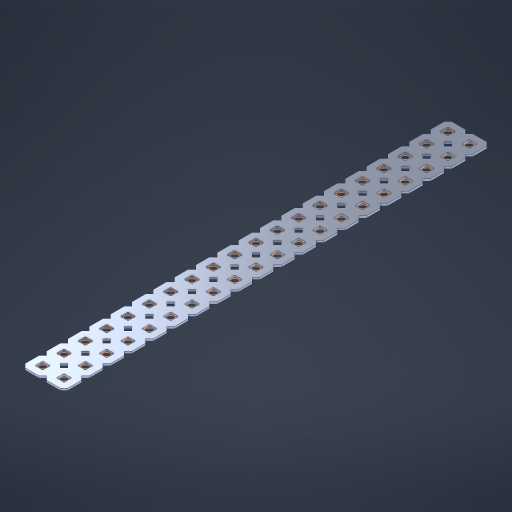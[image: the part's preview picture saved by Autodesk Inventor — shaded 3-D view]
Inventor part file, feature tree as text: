
AUTODESK INVENTOR PART (.ipt)
format: ipt  version: 2023 (Build 270158000, 158)  size: 716,800 bytes
history: native  units: in
note: dims shown in document units (in); Inventor stores cm internally (conversion verified against a paired STEP export)
features: other x41, extrude x39, sketch x2, pattern_linear x1
ambient origin geometry x8: Origin, YZ Plane, XZ Plane, XY Plane, X Axis, Y Axis, Z Axis, Center Point
bodies: Solid1 (feature_tree), Body (feature_tree)
feature tree (83):
  pattern_linear  "Rectangular Pattern1"  Spacing1=0.09in  [1 undecoded]
  sketch  "Sketch1"  dims[d1=0.5in]
  sketch  "Sketch2"  dims[d2=0.182in d3=0.09in d4=0.09in d5=0.09in d6=0.09in d7=0.09in d8=0.09in d9=0.09in d10=0.09in d11=0.02in d13=0.0in d14=0.172in d15=0.0625in d16=0.0in d19=0.5in d22=0.5in]
  other  "Srf1"
  other  "Srf126"
  other  "Srf127"
  other  "Srf128"
  other  "Srf129"
  other  "Srf130"
  other  "Srf131"
  other  "Srf250"
  other  "Srf251"
  other  "Srf252"
  other  "Srf253"
  other  "Srf254"
  other  "Srf255"
  other  "Srf256"
  other  "Srf257"
  other  "Srf258"
  other  "Srf259"
  other  "Srf260"
  other  "Srf261"
  other  "Srf262"
  other  "Srf268"
  other  "Srf269"
  other  "Srf270"
  other  "Srf271"
  other  "Srf272"
  other  "Srf273"
  other  "Srf274"
  other  "Srf275"
  other  "Srf276"
  other  "Srf277"
  other  "Srf278"
  other  "Srf279"
  other  "Srf280"
  other  "Srf281"
  other  "Srf282"
  other  "Srf283"
  other  "Srf284"
  other  "Srf285"
  other  "Srf286"
  other  "Srf287"
  other  "Circle"
  extrude  "ExtrusionSrf126"  Depth=0.09in
  extrude  "ExtrusionSrf127"  Depth=0.09in
  extrude  "ExtrusionSrf128"  Depth=0.09in
  extrude  "ExtrusionSrf129"  Depth=0.09in
  extrude  "ExtrusionSrf130"  Depth=0.09in
  extrude  "ExtrusionSrf131"  Depth=0.09in
  extrude  "ExtrusionSrf250"  Depth=0.09in
  extrude  "ExtrusionSrf251"  Depth=0.02in
  extrude  "ExtrusionSrf252"  TaperAngle=0.0deg  [1 undecoded]
  extrude  "ExtrusionSrf253"  Depth=0.5in
  extrude  "ExtrusionSrf254"  Depth=0.5in TaperAngle=0.0deg
  extrude  "ExtrusionSrf255"  Depth=0.5in
  extrude  "ExtrusionSrf256"  Depth=0.5in
  extrude  "ExtrusionSrf257"  [1 undecoded]
  extrude  "ExtrusionSrf258"  [1 undecoded]
  extrude  "ExtrusionSrf259"  [1 undecoded]
  extrude  "ExtrusionSrf260"  [1 undecoded]
  extrude  "ExtrusionSrf261"  [1 undecoded]
  extrude  "ExtrusionSrf262"  [1 undecoded]
  extrude  "ExtrusionSrf268"  [1 undecoded]
  extrude  "ExtrusionSrf269"  [1 undecoded]
  extrude  "ExtrusionSrf270"  [1 undecoded]
  extrude  "ExtrusionSrf271"  [1 undecoded]
  extrude  "ExtrusionSrf272"  [1 undecoded]
  extrude  "ExtrusionSrf273"  [1 undecoded]
  extrude  "ExtrusionSrf274"  [1 undecoded]
  extrude  "ExtrusionSrf275"  [1 undecoded]
  extrude  "ExtrusionSrf276"  [1 undecoded]
  extrude  "ExtrusionSrf277"  [1 undecoded]
  extrude  "ExtrusionSrf278"  [1 undecoded]
  extrude  "ExtrusionSrf279"  [1 undecoded]
  extrude  "ExtrusionSrf280"  [1 undecoded]
  extrude  "ExtrusionSrf281"  [1 undecoded]
  extrude  "ExtrusionSrf282"  [1 undecoded]
  extrude  "ExtrusionSrf283"  [1 undecoded]
  extrude  "ExtrusionSrf284"  [1 undecoded]
  extrude  "ExtrusionSrf285"  [1 undecoded]
  extrude  "ExtrusionSrf286"  [1 undecoded]
  extrude  "ExtrusionSrf287"  [1 undecoded]
note: 28 required parameter values undecoded (feature->parameter linkage not recoverable at this tier; creation-order binding heuristic only, values carry confidence <= 0.55)
